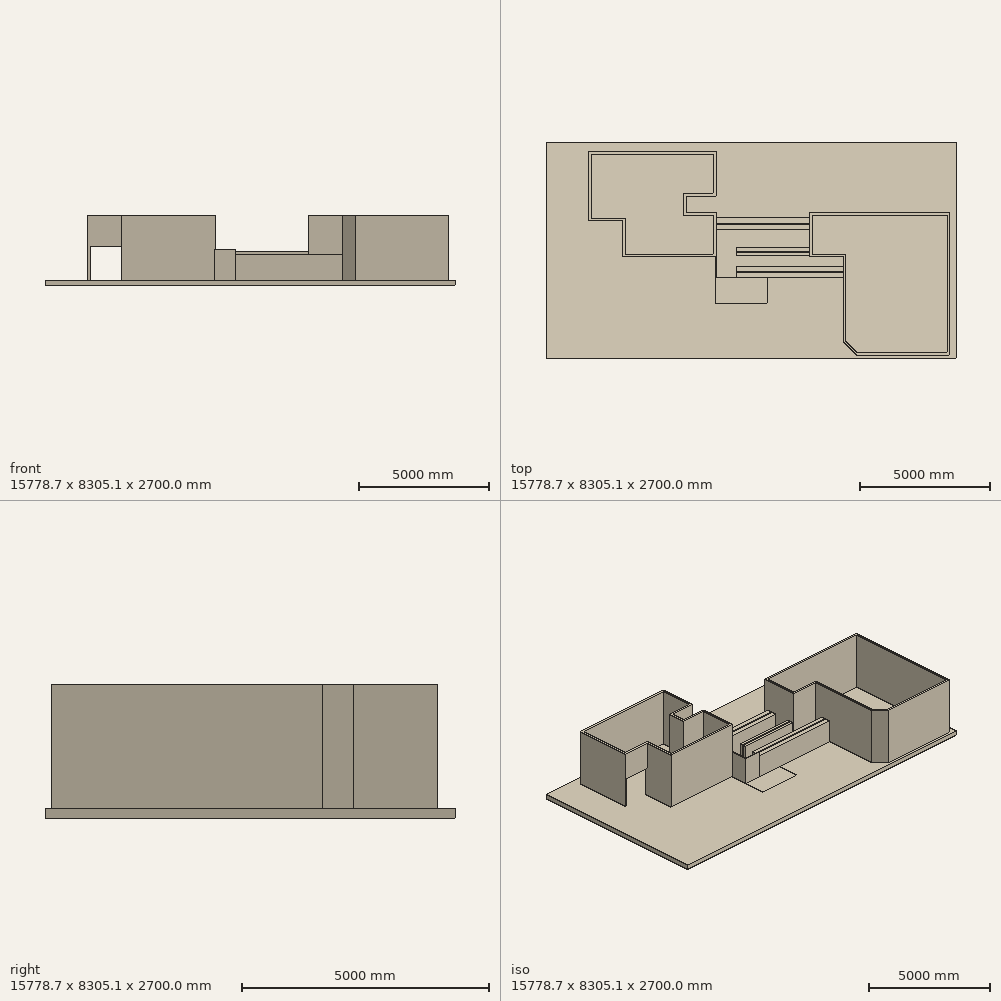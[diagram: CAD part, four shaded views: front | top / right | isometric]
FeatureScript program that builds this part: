
annotation { "Feature Type Name" : "Feature", "Feature Type Description" : "" }
export const myFeature = defineFeature(function(context is Context, id is Id, definition is map)
    precondition{}
    {
        {
            var Q0;
            Q0=qCreatedBy(makeId("Top.planeOp"),FACE);
            var sketch = newSketch(context, id + "F0", { "sketchPlane" : qUnion([Q0])});
            skLineSegment(sketch, "E0", {"start": v(0, 0) * mm, "end": v(3600, 0) * mm});
            skLineSegment(sketch, "E1", {"start": v(3600, 0) * mm, "end": v(3600, 1700) * mm});
            skLineSegment(sketch, "E2.top", {"start": v(100, 100) * mm, "end": v(3500, 100) * mm});
            skLineSegment(sketch, "E2.right", {"start": v(3500, 1600) * mm, "end": v(3500, 100) * mm});
            skLineSegment(sketch, "E3", {"start": v(3600, 1700) * mm, "end": v(2450, 1700) * mm});
            skLineSegment(sketch, "E4", {"start": v(2450, 1700) * mm, "end": v(2450, 2340) * mm});
            skLineSegment(sketch, "E5", {"start": v(2450, 2340) * mm, "end": v(3600, 2340) * mm});
            skLineSegment(sketch, "E6", {"start": v(3600, 2340) * mm, "end": v(3600, 4040) * mm});
            skLineSegment(sketch, "E7", {"start": v(3600, 4040) * mm, "end": v(-1300, 4040) * mm});
            skLineSegment(sketch, "E8", {"start": v(3500, 1600) * mm, "end": v(2340, 1600) * mm});
            skLineSegment(sketch, "E9", {"start": v(2340, 1600) * mm, "end": v(2340, 2440) * mm});
            skLineSegment(sketch, "E10", {"start": v(2340, 2440) * mm, "end": v(3500, 2440) * mm});
            skLineSegment(sketch, "E11", {"start": v(3500, 2440) * mm, "end": v(3500, 3940) * mm});
            skLineSegment(sketch, "E12", {"start": v(3500, 3940) * mm, "end": v(100, 3940) * mm});
            skLineSegment(sketch, "E13", {"start": v(0, 0) * mm, "end": v(0, 1390.88) * mm});
            skLineSegment(sketch, "E14", {"start": v(0, 1390.88) * mm, "end": v(-1300, 1390.88) * mm});
            skLineSegment(sketch, "E15", {"start": v(-1300, 1390.88) * mm, "end": v(-1300, 4040) * mm});
            skLineSegment(sketch, "E16", {"start": v(100, 100) * mm, "end": v(100, 1490.88) * mm});
            skLineSegment(sketch, "E17", {"start": v(100, 1490.88) * mm, "end": v(-1200, 1490.88) * mm});
            skLineSegment(sketch, "E18", {"start": v(-1200, 1490.88) * mm, "end": v(-1200, 3940) * mm});
            skLineSegment(sketch, "E19", {"start": v(100, 3940) * mm, "end": v(-1200, 3940) * mm});
            skSolve(sketch);
        }
        {
            var Q0;
            Q0=makeQuery(id+"F0.imprint","IMPRINT",FACE,{"disambiguationData":[TD([[makeQuery(id+"F0.imprint","IMPRINT",EDGE,{"derivedFrom":sQuery(id+"F0.wireOp",EDGE,"E0")}),1.0]])]});
            extrude(context, id + "F1", {"entities" : qUnion([Q0]), "depth" : 2500 * mm, "offsetDistance" : 25 * mm});
        }
        {
            var Q0;
            Q0=makeQuery(id+"F1.opExtrude","CAP_FACE",FACE,{"disambiguationData":[OSD([sQuery(id+"F0.wireOp",EDGE,"E0"),sQuery(id+"F0.wireOp",EDGE,"E1"),sQuery(id+"F0.wireOp",EDGE,"e1o9Zuh2-btIw-zZZV-bjXi-oInKfqosz957"),sQuery(id+"F0.wireOp",EDGE,"NR816Mve-zncT-idjK-Ag8H-Nvigo6nUvjGr"),sQuery(id+"F0.wireOp",EDGE,"E2.bottom"),sQuery(id+"F0.wireOp",EDGE,"E2.top"),sQuery(id+"F0.wireOp",EDGE,"E2.left"),sQuery(id+"F0.wireOp",EDGE,"E2.right")])],"isStart":true});
            var sketch = newSketch(context, id + "F2", { "sketchPlane" : qUnion([Q0])});
            skLineSegment(sketch, "E20", {"start": v(3600, -1500) * mm, "end": v(7200, -1500) * mm});
            skLineSegment(sketch, "E21", {"start": v(7200, -1500) * mm, "end": v(7200, -1050) * mm});
            skLineSegment(sketch, "E22", {"start": v(7200, -1050) * mm, "end": v(3600, -1050) * mm});
            skLineSegment(sketch, "E23", {"start": v(4400, -345) * mm, "end": v(7200, -345) * mm});
            skLineSegment(sketch, "E24", {"start": v(7200, -345) * mm, "end": v(7200, -45) * mm});
            skLineSegment(sketch, "E25", {"start": v(7200, -45) * mm, "end": v(4400, -45) * mm});
            skLineSegment(sketch, "E26", {"start": v(4400, -45) * mm, "end": v(4400, -345) * mm});
            skLineSegment(sketch, "E27", {"start": v(4400, 805) * mm, "end": v(8500, 805) * mm});
            skLineSegment(sketch, "E28", {"start": v(8500, 805) * mm, "end": v(8500, 355) * mm});
            skLineSegment(sketch, "E29", {"start": v(8500, 355) * mm, "end": v(4400, 355) * mm});
            skLineSegment(sketch, "E30", {"start": v(4400, 355) * mm, "end": v(4400, 805) * mm});
            skSolve(sketch);
        }
        {
            var Q0;
            Q0=makeQuery(id+"F2.imprint","IMPRINT",FACE,{"disambiguationData":[TD([[makeQuery(id+"F2.imprint","IMPRINT",EDGE,{"derivedFrom":sQuery(id+"F2.wireOp",EDGE,"E27")}),-1.0]])]});
            var Q1;
            {var subQ0=sQuery(id+"F2.wireOp",EDGE,"E20");Q1=makeQuery(id+"F2.imprint","IMPRINT",FACE,{"disambiguationData":[TD([[makeQuery(id+"F2.imprint","IMPRINT",EDGE,{"derivedFrom":subQ0}),1.0]])]});}
            var Q2;
            Q2=makeQuery(id+"F2.imprint","IMPRINT",FACE,{"disambiguationData":[TD([[makeQuery(id+"F2.imprint","IMPRINT",EDGE,{"derivedFrom":sQuery(id+"F2.wireOp",EDGE,"E23")}),1.0]])]});
            extrude(context, id + "F3", {"entities" : qUnion([Q0, Q1, Q2]), "oppositeDirection" : true, "depth" : 1100 * mm, "offsetDistance" : 25 * mm});
        }
        {
            var Q0;
            Q0=makeQuery(id+"F3.opExtrude","CAP_FACE",FACE,{"disambiguationData":[OSD([sQuery(id+"F2.wireOp",EDGE,"E27"),sQuery(id+"F2.wireOp",EDGE,"E28"),sQuery(id+"F2.wireOp",EDGE,"E29"),sQuery(id+"F2.wireOp",EDGE,"E30")])],"isStart":true});
            var sketch = newSketch(context, id + "F4", { "sketchPlane" : qUnion([Q0])});
            skLineSegment(sketch, "E31", {"start": v(7200, -1700) * mm, "end": v(7200, 0) * mm});
            skLineSegment(sketch, "E32", {"start": v(7200, 0) * mm, "end": v(8500, 0) * mm});
            skLineSegment(sketch, "E33", {"start": v(8500, 0) * mm, "end": v(8500, 3280) * mm});
            skLineSegment(sketch, "E34", {"start": v(7200, -1700) * mm, "end": v(12594.97, -1700) * mm});
            skLineSegment(sketch, "E35", {"start": v(7300, -1600) * mm, "end": v(12494.97, -1600) * mm});
            skLineSegment(sketch, "E36", {"start": v(8600, 3238.58) * mm, "end": v(8600, -100) * mm});
            skLineSegment(sketch, "E37", {"start": v(8600, -100) * mm, "end": v(7300, -100) * mm});
            skLineSegment(sketch, "E38", {"start": v(7300, -1600) * mm, "end": v(7300, -100) * mm});
            skLineSegment(sketch, "E39", {"start": v(8500, 3280) * mm, "end": v(8994.97, 3774.97) * mm});
            skLineSegment(sketch, "E40", {"start": v(8994.97, 3774.97) * mm, "end": v(12594.97, 3774.97) * mm});
            skLineSegment(sketch, "E41", {"start": v(12594.97, 3774.97) * mm, "end": v(12594.97, -1700) * mm});
            skLineSegment(sketch, "E42", {"start": v(8600, 3238.58) * mm, "end": v(9036.4, 3674.97) * mm});
            skLineSegment(sketch, "E43", {"start": v(12494.97, -1600) * mm, "end": v(12494.97, 3674.97) * mm});
            skLineSegment(sketch, "E44", {"start": v(12494.97, 3674.97) * mm, "end": v(9036.4, 3674.97) * mm});
            skSolve(sketch);
        }
        {
            var Q0;
            Q0 = qSketchRegion(id + "F4", true);
            extrude(context, id + "F5", {"entities" : qUnion([Q0]), "oppositeDirection" : true, "depth" : 2500 * mm, "offsetDistance" : 25 * mm});
        }
        {
            var Q0;
            Q0=makeQuery(id+"F3.opExtrude","CAP_FACE",FACE,{"disambiguationData":[OSD([sQuery(id+"F2.wireOp",EDGE,"E27"),sQuery(id+"F2.wireOp",EDGE,"E28"),sQuery(id+"F2.wireOp",EDGE,"E29"),sQuery(id+"F2.wireOp",EDGE,"E30")])],"isStart":true});
            var sketch = newSketch(context, id + "F6", { "sketchPlane" : qUnion([Q0])});
            skLineSegment(sketch, "E45.bottom", {"start": v(12854.77, 3905.37) * mm, "end": v(-2923.92, 3905.37) * mm});
            skLineSegment(sketch, "E45.top", {"start": v(12854.77, -4399.7) * mm, "end": v(-2923.92, -4399.7) * mm});
            skLineSegment(sketch, "E45.left", {"start": v(12854.77, 3905.37) * mm, "end": v(12854.77, -4399.7) * mm});
            skLineSegment(sketch, "E45.right", {"start": v(-2923.92, 3905.37) * mm, "end": v(-2923.92, -4399.7) * mm});
            skSolve(sketch);
        }
        {
            var Q0;
            Q0 = qSketchRegion(id + "F6", true);
            extrude(context, id + "F7", {"entities" : qUnion([Q0]), "depth" : 200 * mm, "offsetDistance" : 25 * mm});
        }
        {
            var Q0;
            Q0=makeQuery(id+"F3.opExtrude","CAP_FACE",FACE,{"disambiguationData":[OSD([sQuery(id+"F2.wireOp",EDGE,"E27"),sQuery(id+"F2.wireOp",EDGE,"E28"),sQuery(id+"F2.wireOp",EDGE,"E29"),sQuery(id+"F2.wireOp",EDGE,"E30")])],"isStart":false});
            var sketch = newSketch(context, id + "F8", { "sketchPlane" : qUnion([Q0])});
            skLineSegment(sketch, "E46", {"start": v(4400, -599.96) * mm, "end": v(4400, -550) * mm});
            skLineSegment(sketch, "E47", {"start": v(4400, -550) * mm, "end": v(8500, -550) * mm});
            skLineSegment(sketch, "E48", {"start": v(8500, -550) * mm, "end": v(8500, -600) * mm});
            skLineSegment(sketch, "E49", {"start": v(8500, -600) * mm, "end": v(4400, -600) * mm});
            skLineSegment(sketch, "E50", {"start": v(4400, 220) * mm, "end": v(7200, 220) * mm});
            skLineSegment(sketch, "E51", {"start": v(7200, 220) * mm, "end": v(7200, 170) * mm});
            skLineSegment(sketch, "E52", {"start": v(7200, 170) * mm, "end": v(4400, 170) * mm});
            skLineSegment(sketch, "E53", {"start": v(4400, 170) * mm, "end": v(4400, 220) * mm});
            skLineSegment(sketch, "E54", {"start": v(3600, 1300) * mm, "end": v(7200, 1300) * mm});
            skLineSegment(sketch, "E55", {"start": v(7200, 1300) * mm, "end": v(7200, 1250) * mm});
            skLineSegment(sketch, "E56", {"start": v(7200, 1250) * mm, "end": v(3600, 1250) * mm});
            skLineSegment(sketch, "E57", {"start": v(3600, 1250) * mm, "end": v(3600, 1300) * mm});
            skSolve(sketch);
        }
        {
            var Q0;
            {var subQ1=sQuery(id+"F8.wireOp",EDGE,"E46");Q0=makeQuery(id+"F8.imprint","IMPRINT",FACE,{"disambiguationData":[TD([[makeQuery(id+"F8.imprint","IMPRINT",EDGE,{"derivedFrom":subQ1}),1.0]])]});}
            var Q1;
            Q1=makeQuery(id+"F8.imprint","IMPRINT",FACE,{"disambiguationData":[TD([[makeQuery(id+"F8.imprint","IMPRINT",EDGE,{"derivedFrom":sQuery(id+"F8.wireOp",EDGE,"E50")}),-1.0]])]});
            var Q2;
            Q2=makeQuery(id+"F8.imprint","IMPRINT",FACE,{"disambiguationData":[TD([[makeQuery(id+"F8.imprint","IMPRINT",EDGE,{"derivedFrom":sQuery(id+"F8.wireOp",EDGE,"E54")}),-1.0]])]});
            extrude(context, id + "F9", {"entities" : qUnion([Q0, Q1, Q2]), "operationType" : NewBodyOperationType.REMOVE, "oppositeDirection" : true, "depth" : 700 * mm, "offsetDistance" : 25 * mm});
        }
        {
            var Q0;
            Q0=makeQuery(id+"F3.opExtrude","SWEPT_FACE",FACE,{"disambiguationData":[OSD([sQuery(id+"F2.wireOp",EDGE,"E30")])]});
            var sketch = newSketch(context, id + "F10", { "sketchPlane" : qUnion([Q0])});
            skLineSegment(sketch, "E58", {"start": v(355, 1100) * mm, "end": v(805, 1100) * mm});
            skLineSegment(sketch, "E59", {"start": v(805, 1100) * mm, "end": v(805, 1000) * mm});
            skLineSegment(sketch, "E60", {"start": v(805, 1000) * mm, "end": v(355, 1000) * mm});
            skLineSegment(sketch, "E61", {"start": v(355, 1000) * mm, "end": v(355, 1100) * mm});
            skSolve(sketch);
        }
        {
            var Q0;
            {var subQ0=sQuery(id+"F10.wireOp",EDGE,"E59");Q0=makeQuery(id+"F10.imprint","IMPRINT",FACE,{"disambiguationData":[TD([[makeQuery(id+"F10.imprint","IMPRINT",EDGE,{"derivedFrom":subQ0}),-1.0]])]});}
            var Q1;
            {var subQ0=sQuery(id+"F10.wireOp",EDGE,"E58");var subQ1=sQuery(id+"F2.wireOp",EDGE,"E30");var subQ4=makeQuery(id+"F9.boolean.opBoolean","COPY",EDGE,{"derivedFrom":makeQuery(id+"F9.opExtrude","SWEPT_EDGE",EDGE,{"disambiguationData":[OSD([subQ1,sQuery(id+"F8.wireOp",EDGE,"E49")])]})});var subQ5=makeQuery(id+"F10.imprint","INTERSECT",VERTEX,{"derivedFrom":[subQ4,subQ0]});Q1=makeQuery(id+"F10.imprint","IMPRINT",FACE,{"disambiguationData":[TD([[makeQuery(id+"F10.imprint","IMPRINT",EDGE,{"disambiguationData":[TD([[subQ5,1.0]])],"derivedFrom":subQ0}),-1.0]])]});}
            var Q2;
            {var subQ0=sQuery(id+"F10.wireOp",EDGE,"E61");Q2=makeQuery(id+"F10.imprint","IMPRINT",FACE,{"disambiguationData":[TD([[makeQuery(id+"F10.imprint","IMPRINT",EDGE,{"derivedFrom":subQ0}),1.0]])]});}
            var Q3;
            Q3=makeQuery(id+"F5.opExtrude","SWEPT_FACE",FACE,{"disambiguationData":[OSD([sQuery(id+"F4.wireOp",EDGE,"E33")])]});
            extrude(context, id + "F11", {"entities" : qUnion([Q0, Q1, Q2]), "operationType" : NewBodyOperationType.REMOVE, "endBound" : BoundingType.UP_TO_SURFACE, "oppositeDirection" : true, "depth" : 25 * mm, "endBoundEntityFace" : qUnion([Q3]), "offsetDistance" : 25 * mm});
        }
        {
            var Q0;
            Q0=makeQuery(id+"F7.opExtrude","CAP_FACE",FACE,{"disambiguationData":[OSD([sQuery(id+"F6.wireOp",EDGE,"E45.bottom"),sQuery(id+"F6.wireOp",EDGE,"E45.top"),sQuery(id+"F6.wireOp",EDGE,"E45.left"),sQuery(id+"F6.wireOp",EDGE,"E45.right")])],"isStart":true});
            var sketch = newSketch(context, id + "F12", { "sketchPlane" : qUnion([Q0])});
            skLineSegment(sketch, "E62", {"start": v(4400, -805) * mm, "end": v(3590, -805) * mm});
            skLineSegment(sketch, "E63", {"start": v(3600, -795) * mm, "end": v(3600, 0) * mm});
            skLineSegment(sketch, "E64", {"start": v(3590, 0) * mm, "end": v(3590, -805) * mm});
            skLineSegment(sketch, "E65", {"start": v(4400, -795) * mm, "end": v(3600, -795) * mm});
            skLineSegment(sketch, "E66", {"start": v(3590, 0) * mm, "end": v(3600, 0) * mm});
            skLineSegment(sketch, "E67", {"start": v(4400, -795) * mm, "end": v(4400, -805) * mm});
            skSolve(sketch);
        }
        {
            var Q0;
            Q0 = qSketchRegion(id + "F12", true);
            extrude(context, id + "F13", {"entities" : qUnion([Q0]), "depth" : 1200 * mm, "offsetDistance" : 25 * mm});
        }
        {
            var Q0;
            Q0=makeQuery(id+"F7.opExtrude","CAP_FACE",FACE,{"disambiguationData":[OSD([sQuery(id+"F6.wireOp",EDGE,"E45.bottom"),sQuery(id+"F6.wireOp",EDGE,"E45.top"),sQuery(id+"F6.wireOp",EDGE,"E45.left"),sQuery(id+"F6.wireOp",EDGE,"E45.right")])],"isStart":true});
            var sketch = newSketch(context, id + "F14", { "sketchPlane" : qUnion([Q0])});
            skLineSegment(sketch, "E68.bottom", {"start": v(3590, -805) * mm, "end": v(5590, -805) * mm});
            skLineSegment(sketch, "E68.top", {"start": v(3590, -1805) * mm, "end": v(5590, -1805) * mm});
            skLineSegment(sketch, "E68.left", {"start": v(3590, -805) * mm, "end": v(3590, -1805) * mm});
            skLineSegment(sketch, "E68.right", {"start": v(5590, -805) * mm, "end": v(5590, -1805) * mm});
            skSolve(sketch);
        }
        {
            var Q0;
            Q0 = qSketchRegion(id + "F14", true);
            extrude(context, id + "F15", {"entities" : qUnion([Q0]), "operationType" : NewBodyOperationType.REMOVE, "oppositeDirection" : true, "depth" : 3 * mm, "offsetDistance" : 25 * mm});
        }
        {
            var Q0;
            Q0=makeQuery(id+"F1.opExtrude","SWEPT_FACE",FACE,{"disambiguationData":[OSD([sQuery(id+"F0.wireOp",EDGE,"E14")])]});
            var sketch = newSketch(context, id + "F16", { "sketchPlane" : qUnion([Q0])});
            skLineSegment(sketch, "E69.bottom", {"start": v(-1205.43, 0) * mm, "end": v(0, 0) * mm});
            skLineSegment(sketch, "E69.top", {"start": v(-1205.43, 1300) * mm, "end": v(0, 1300) * mm});
            skLineSegment(sketch, "E69.left", {"start": v(-1205.43, 0) * mm, "end": v(-1205.43, 1300) * mm});
            skLineSegment(sketch, "E69.right", {"start": v(0, 0) * mm, "end": v(0, 1300) * mm});
            skSolve(sketch);
        }
        {
            var Q0;
            Q0 = qSketchRegion(id + "F16", true);
            extrude(context, id + "F17", {"entities" : qUnion([Q0]), "operationType" : NewBodyOperationType.REMOVE, "oppositeDirection" : true, "depth" : 6000 * mm, "offsetDistance" : 25 * mm});
        }
    });
